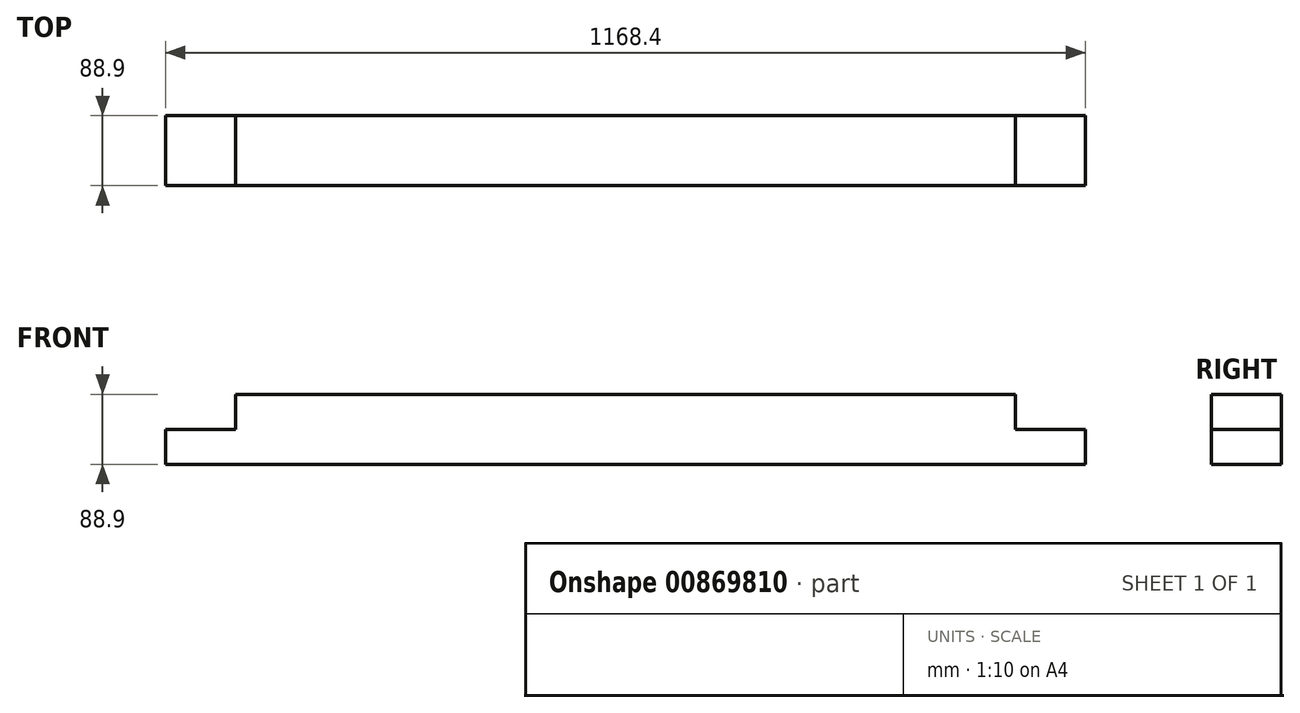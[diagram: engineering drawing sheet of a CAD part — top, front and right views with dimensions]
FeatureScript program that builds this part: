
annotation { "Feature Type Name" : "Feature", "Feature Type Description" : "" }
export const myFeature = defineFeature(function(context is Context, id is Id, definition is map)
    precondition{}
    {
        {
            var Q0;
            Q0=qCreatedBy(makeId("Right.planeOp"),FACE);
            var sketch = newSketch(context, id + "F0", { "sketchPlane" : qUnion([Q0])});
            skLineSegment(sketch, "E0.bottom", {"start": v(-44.45, 44.45) * mm, "end": v(44.45, 44.45) * mm});
            skLineSegment(sketch, "E0.top", {"start": v(-44.45, -44.45) * mm, "end": v(44.45, -44.45) * mm});
            skLineSegment(sketch, "E0.left", {"start": v(-44.45, 44.45) * mm, "end": v(-44.45, -44.45) * mm});
            skLineSegment(sketch, "E0.right", {"start": v(44.45, 44.45) * mm, "end": v(44.45, -44.45) * mm});
            skPoint(sketch, "E0.middle", {"position": v(0, 0) * mm});
            skSolve(sketch);
        }
        {
            var Q0;
            Q0 = qSketchRegion(id + "F0", true);
            extrude(context, id + "F1", {"entities" : qUnion([Q0]), "endBound" : BoundingType.SYMMETRIC, "depth" : 1346.2 * mm, "offsetDistance" : 25.4 * mm});
        }
        {
            var Q0;
            Q0=makeQuery(id+"F1.opExtrude","SWEPT_FACE",FACE,{"disambiguationData":[OSD([sQuery(id+"F0.wireOp",EDGE,"E0.left")])]});
            var sketch = newSketch(context, id + "F2", { "sketchPlane" : qUnion([Q0])});
            skLineSegment(sketch, "E1.bottom", {"start": v(-584.2, 44.45) * mm, "end": v(-495.3, 44.45) * mm});
            skLineSegment(sketch, "E1.top", {"start": v(-584.2, 0) * mm, "end": v(-495.3, 0) * mm});
            skLineSegment(sketch, "E1.left", {"start": v(-584.2, 44.45) * mm, "end": v(-584.2, 0) * mm});
            skLineSegment(sketch, "E1.right", {"start": v(-495.3, 44.45) * mm, "end": v(-495.3, 0) * mm});
            skLineSegment(sketch, "E2", {"start": v(0, 44.45) * mm, "end": v(0, -44.45) * mm, "construction": true});
            skLineSegment(sketch, "E3.MirrorCS", {"start": v(584.2, 44.45) * mm, "end": v(495.3, 44.45) * mm});
            skLineSegment(sketch, "E4.MirrorCS", {"start": v(495.3, 44.45) * mm, "end": v(495.3, 0) * mm});
            skLineSegment(sketch, "E5.MirrorCS", {"start": v(584.2, 0) * mm, "end": v(495.3, 0) * mm});
            skLineSegment(sketch, "E6.MirrorCS", {"start": v(584.2, 44.45) * mm, "end": v(584.2, 0) * mm});
            skSolve(sketch);
        }
        {
            var Q0;
            Q0 = qSketchRegion(id + "F2", true);
            extrude(context, id + "F3", {"entities" : qUnion([Q0]), "operationType" : NewBodyOperationType.REMOVE, "endBound" : BoundingType.THROUGH_ALL, "oppositeDirection" : true, "depth" : 25.4 * mm, "offsetDistance" : 25.4 * mm});
        }
        {
            var Q0;
            Q0=makeQuery(id+"F1.opExtrude","SWEPT_FACE",FACE,{"disambiguationData":[OSD([sQuery(id+"F0.wireOp",EDGE,"E0.left")])]});
            var sketch = newSketch(context, id + "F4", { "sketchPlane" : qUnion([Q0])});
            skLineSegment(sketch, "E7.bottom", {"start": v(-584.2, 44.45) * mm, "end": v(-673.1, 44.45) * mm});
            skLineSegment(sketch, "E7.top", {"start": v(-584.2, -44.45) * mm, "end": v(-673.1, -44.45) * mm});
            skLineSegment(sketch, "E7.left", {"start": v(-584.2, 44.45) * mm, "end": v(-584.2, -44.45) * mm});
            skLineSegment(sketch, "E7.right", {"start": v(-673.1, 44.45) * mm, "end": v(-673.1, -44.45) * mm});
            skLineSegment(sketch, "E8.bottom", {"start": v(584.2, 44.45) * mm, "end": v(673.1, 44.45) * mm});
            skLineSegment(sketch, "E8.top", {"start": v(584.2, -44.45) * mm, "end": v(673.1, -44.45) * mm});
            skLineSegment(sketch, "E8.left", {"start": v(584.2, 44.45) * mm, "end": v(584.2, -44.45) * mm});
            skLineSegment(sketch, "E8.right", {"start": v(673.1, 44.45) * mm, "end": v(673.1, -44.45) * mm});
            skSolve(sketch);
        }
        {
            var Q0;
            Q0 = qSketchRegion(id + "F4", true);
            extrude(context, id + "F5", {"entities" : qUnion([Q0]), "operationType" : NewBodyOperationType.REMOVE, "endBound" : BoundingType.THROUGH_ALL, "oppositeDirection" : true, "depth" : 25.4 * mm, "offsetDistance" : 25.4 * mm});
        }
    });
